# Revit family: Doors_Shutters_Overhead-Door-Corporation_Allura-Shutter-Door​​-653_
name_source: partatom
category: Specialty Equipment
units: mm (PartAtom-declared; Revit-internal decimal feet)

## family parameters
Always vertical = Yes
Cut with Voids When Loaded = Yes
Host = Wall
OmniClass Number = 23.30.10.21.34
OmniClass Title = Industrial Doors
Part Type = Normal
Room Calculation Point = No
Round Connector Dimension = Use Diameter
Shared = No

## types (4) — shared parameters
Connector Array Distance = 0' - 0"
Description = Allura Shutter Model 653 Rolling Security Door
Hood Offset = 0' - 2"
Manufacturer = Overhead Door Corporation
Model = 653
Number of Poles = 1
Powder Coat (Note) = PowderGuard® Premium powder coat finish options are available in approximately 200 colors and can be custom matched to architect specifications.
Product Guid = 91723a56-d4a4-4d33-84ad-b2c2c72e9cdc
Product Page URL = https://www.overheaddoor.com
Product data url = https://www.bimobject.com
URL = https://www.overheaddoor.com
Wall Closure = By host

## per-type parameters (varying)
| type | Apparent Load Phase 1 | Connector Array | Crank | Crank + Tube Motor | Current | Frequency | Manual | Power Factor | Tube Motor | Voltage |
| 115 volts, one phase, 60 Hz (110-120V range) | 2300 VA | 3 | No | Yes | 20 A | 60 Hz | No | 1 | Yes | 115 V |
| Manual push-up | 0 VA | 2 | No | No | 0 A | 0 Hz | Yes | 1 | No | 0 V |
| 240 volts, one phase, 60 Hz (208-245V range) | 4800 VA | 3 | No | Yes | 20 A | 60 Hz | No | 1 | Yes | 240 V |
| Manual crank | 0 VA | 2 | Yes | Yes | 0 A | 0 Hz | No | 0 | No | 0 V |

## geometry (parser evidence)
native form markers: Sweep x8
no freeform markers — native parametric forms only
